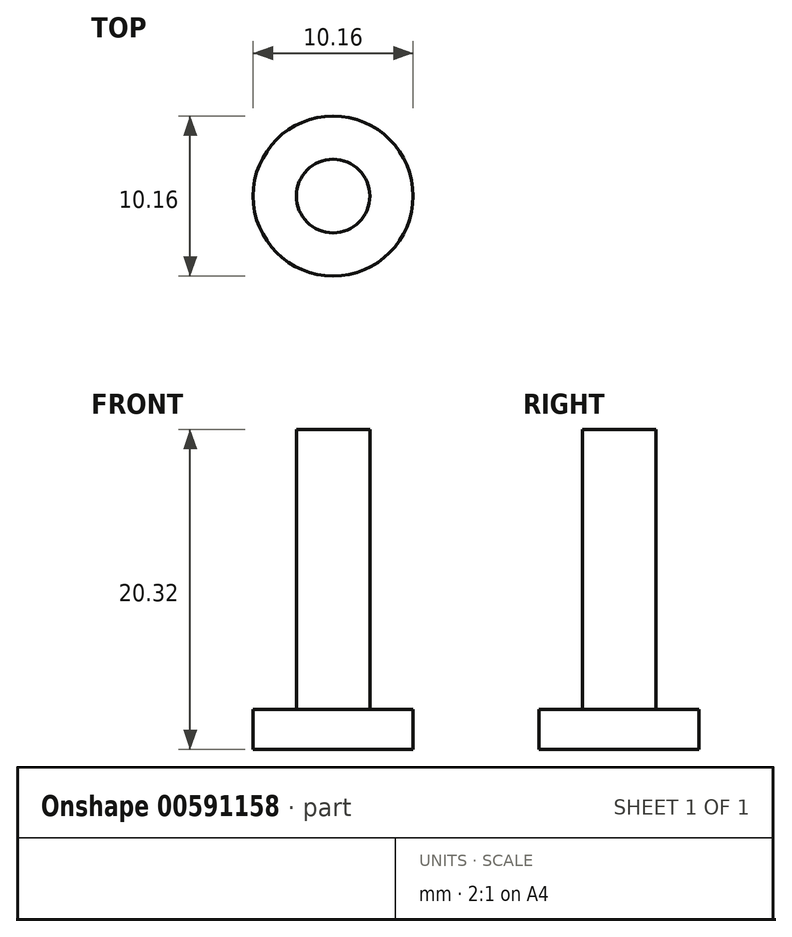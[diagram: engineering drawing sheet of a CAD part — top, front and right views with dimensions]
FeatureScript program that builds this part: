
annotation { "Feature Type Name" : "Feature", "Feature Type Description" : "" }
export const myFeature = defineFeature(function(context is Context, id is Id, definition is map)
    precondition{}
    {
        {
            var Q0;
            Q0=qCreatedBy(makeId("Top.planeOp"),FACE);
            var sketch = newSketch(context, id + "F0", { "sketchPlane" : qUnion([Q0])});
            skCircle(sketch, "E0", {"center": v(0, 0) * mm, "radius": 2.33 * mm});
            skSolve(sketch);
        }
        {
            var Q0;
            Q0=makeQuery(id+"F0.imprint","IMPRINT",FACE,{"disambiguationData":[TD([[makeQuery(id+"F0.imprint","IMPRINT",EDGE,{"derivedFrom":sQuery(id+"F0.wireOp",EDGE,"E0")}),1.0]])]});
            extrude(context, id + "F1", {"entities" : qUnion([Q0]), "depth" : 17.78 * mm, "offsetDistance" : 25.4 * mm});
        }
        {
            var Q0;
            Q0=makeQuery(id+"F1.opExtrude","CAP_FACE",FACE,{"disambiguationData":[OSD([sQuery(id+"F0.wireOp",EDGE,"E0")])],"isStart":true});
            var sketch = newSketch(context, id + "F2", { "sketchPlane" : qUnion([Q0])});
            skCircle(sketch, "E1", {"center": v(0, 0) * mm, "radius": 5.08 * mm});
            skSolve(sketch);
        }
        {
            var Q0;
            Q0=makeQuery(id+"F2.imprint","IMPRINT",FACE,{"disambiguationData":[TD([[makeQuery(id+"F2.imprint","IMPRINT",EDGE,{"derivedFrom":sQuery(id+"F2.wireOp",EDGE,"E1")}),1.0]])]});
            var Q1;
            Q1=makeQuery(id+"F2.imprint","IMPRINT",FACE,{"disambiguationData":[TD([[makeQuery(id+"F2.imprint","IMPRINT",EDGE,{"derivedFrom":makeQuery(id+"F1.opExtrude","CAP_EDGE",EDGE,{"disambiguationData":[OSD([sQuery(id+"F0.wireOp",EDGE,"E0")])],"isStart":true})}),-1.0]])]});
            extrude(context, id + "F3", {"entities" : qUnion([Q0, Q1]), "operationType" : NewBodyOperationType.ADD, "depth" : 2.54 * mm, "offsetDistance" : 25.4 * mm});
        }
    });
